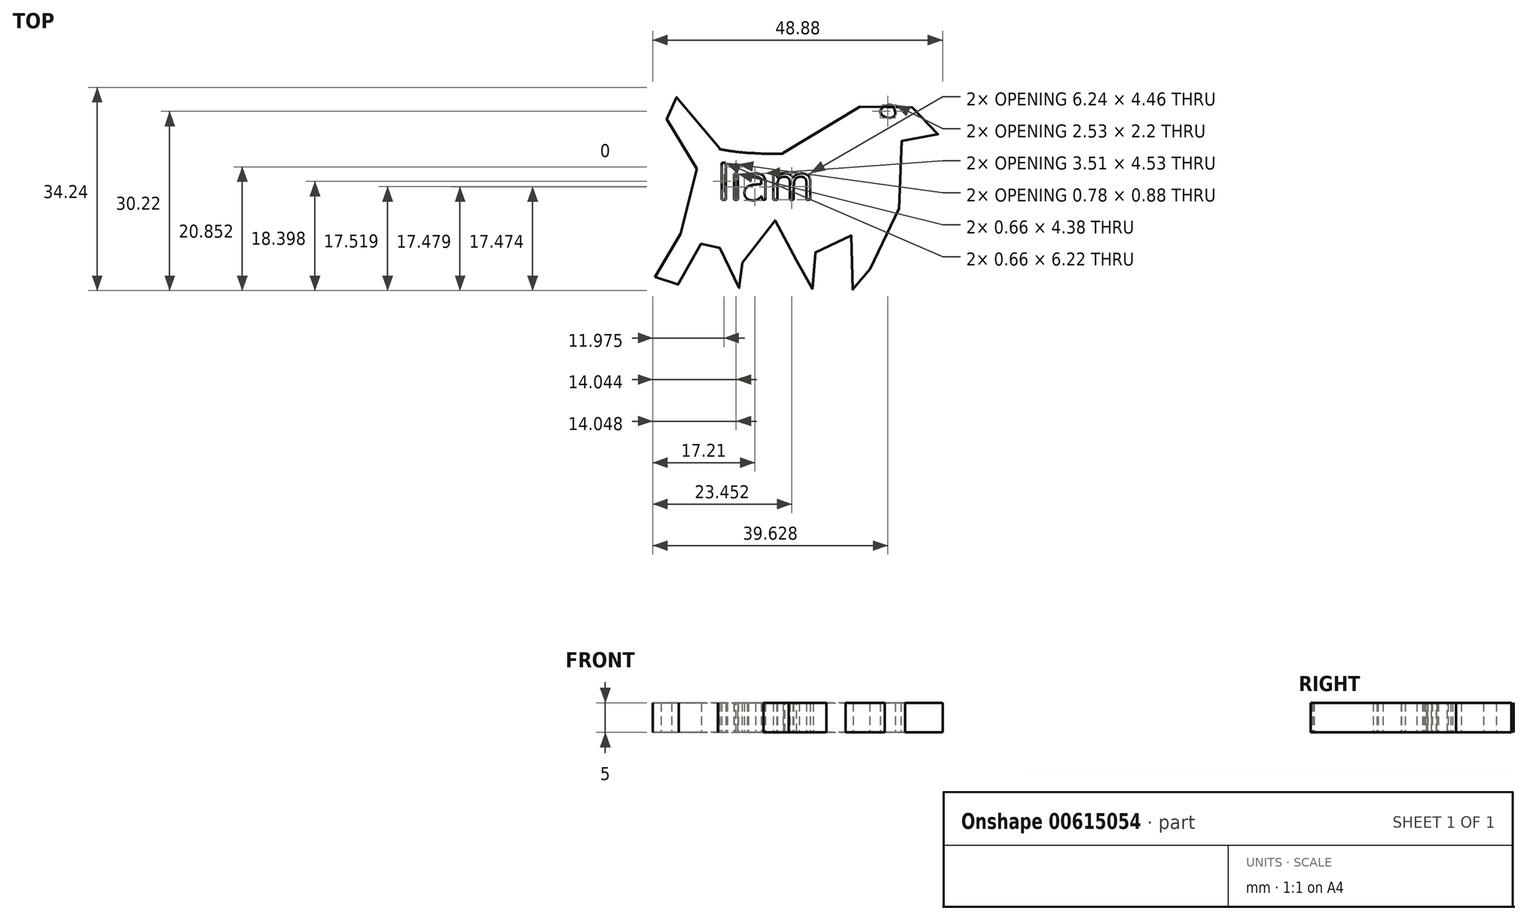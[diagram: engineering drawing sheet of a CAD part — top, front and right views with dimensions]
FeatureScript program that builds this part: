
annotation { "Feature Type Name" : "Feature", "Feature Type Description" : "" }
export const myFeature = defineFeature(function(context is Context, id is Id, definition is map)
    precondition{}
    {
        {
            var Q0;
            Q0=qCreatedBy(makeId("Top.planeOp"),FACE);
            var sketch = newSketch(context, id + "F0", { "sketchPlane" : qUnion([Q0])});
            skFitSpline(sketch, "E0", {"points": [v(-50.92, 47.75) * mm, v(-52.4, 46.1) * mm, v(-52.2, 44.07) * mm, v(-49.26, 38.73) * mm, v(-45.77, 35.6) * mm, v(-46.87, 33.4) * mm, v(-47.42, 28.8) * mm, v(-49.26, 23.1) * mm, v(-51.84, 20.7) * mm, v(-52.57, 17.76) * mm, v(-53.68, 15.55) * mm, v(-53.86, 14.08) * mm, v(-52.94, 14.08) * mm, v(-49.81, 13.9) * mm, v(-49.63, 14.44) * mm, v(-50.73, 15.55) * mm, v(-49.45, 17.76) * mm, v(-45.58, 21.62) * mm, v(-41.9, 24.01) * mm, v(-41.53, 22.54) * mm, v(-42.45, 21.07) * mm, v(-42.64, 17.2) * mm, v(-41.17, 15.55) * mm, v(-40.61, 14.26) * mm, v(-35.28, 14.44) * mm, v(-37.85, 16.1) * mm, v(-38.77, 18.3) * mm, v(-36.01, 22.17) * mm, v(-34.54, 25.67) * mm, v(-31.78, 24.75) * mm, v(-30.13, 24.75) * mm, v(-29.4, 19.6) * mm, v(-30.68, 17.2) * mm, v(-30.68, 14.08) * mm, v(-28.29, 13.9) * mm, v(-24.8, 13.7) * mm, v(-24.8, 14.26) * mm, v(-26.63, 15.92) * mm, v(-24.42, 24.2) * mm, v(-22.03, 24.56) * mm, v(-21.11, 24.2) * mm, v(-20.2, 19.96) * mm, v(-21.3, 15.92) * mm, v(-20.74, 13.9) * mm, v(-15.4, 13.9) * mm, v(-14.86, 14.26) * mm, v(-16.88, 15.73) * mm, v(-15.78, 24.38) * mm, v(-13.75, 25.85) * mm, v(-11.54, 29.53) * mm, v(-11.91, 35.24) * mm, v(-11.73, 38.92) * mm, v(-10.26, 38) * mm, v(-9.15, 38.73) * mm, v(-6.76, 39.1) * mm, v(-5.1, 42.04) * mm, v(-7.13, 42.96) * mm, v(-9.15, 43.33) * mm, v(-12.1, 46.46) * mm, v(-16.33, 47.01) * mm, v(-19.64, 43.33) * mm, v(-23.32, 38.36) * mm, v(-42.64, 37.44) * mm, v(-45.03, 39.47) * mm, v(-49.26, 44.62) * mm, v(-50.92, 47.75) * mm]});
            skFitSpline(sketch, "E1", {"points": [v(-42.64, 37.44) * mm, v(-36.57, 36.66) * mm, v(-31.98, 36.7) * mm, v(-42.64, 37.44) * mm]});
            skText(sketch, "E2", { "text": "liam", "fontName": "OpenSans-Regular.ttf"});
            skFitSpline(sketch, "E3", {"points": [v(-13.9, 44.83) * mm, v(-15.55, 43.9) * mm, v(-14.76, 42.75) * mm, v(-13.17, 42.97) * mm, v(-13.18, 44.06) * mm, v(-13.9, 44.83) * mm]});
            const initialGuessF0  = {"E2": [-0.043, 0.0288, 1, 0, 0.00589]};
            skSetInitialGuess(sketch, initialGuessF0);
            skSolve(sketch);
        }
        {
            var Q0;
            {var subQ0=sQuery(id+"F0.wireOp",EDGE,"E1");var subQ1=sQuery(id+"F0.wireOp",EDGE,"E0");var subQ2=makeQuery(id+"F0.imprint","INTERSECT",VERTEX,{"disambiguationData":[OD(2.0)],"derivedFrom":[subQ1,subQ0]});Q0=makeQuery(id+"F0.imprint","IMPRINT",FACE,{"disambiguationData":[TD([[makeQuery(id+"F0.imprint","IMPRINT",EDGE,{"disambiguationData":[TD([[subQ2,-1.0]])],"derivedFrom":subQ1}),1.0]])]});}
            extrude(context, id + "F1", {"entities" : qUnion([Q0]), "depth" : 5 * mm, "offsetDistance" : 25 * mm});
        }
    });
